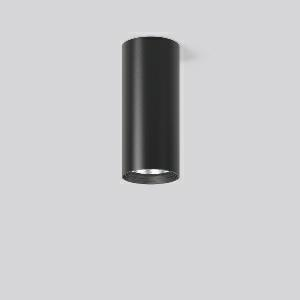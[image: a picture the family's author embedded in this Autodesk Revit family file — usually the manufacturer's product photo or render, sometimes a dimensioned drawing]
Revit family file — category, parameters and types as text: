
# Revit family: heledon_mini_a_931200_003_4768
name_source: partatom
category: Lighting Fixtures
units: mm (PartAtom-declared; Revit-internal decimal feet)

## family parameters
Cut with Voids When Loaded = No
Host = Face
Light Source = No
Part Type = Normal
Room Calculation Point = No
Round Connector Dimension = Use Diameter
Shared = No

## types (1)
- HELEDON mini A (1 x LED Modul 930, 2500 lm, 3000)
    Apparent Load = 20 VA
    Approval mark = CE
    CIE Flux Codes = 100 100 100 100 100
    Color Rendering = 90
    Color Temperature = 3000
    Default Elevation = 1800 mm
    Description = Series: HELEDON mini
Cylindrical surface-mounted downlight. Housing: die-cast aluminium, powder-coated. Internal ceiling frame polycarbonate with bayonet mounting. Black plastic ring and recessed LED to prevent glare from the side. Optical assembly with reflector made of MIRO-Silver with 98% total light reflection for outstanding efficiency - can be changed without tools. Best colour rendering index Ra>90. Suitable for Ceiling mounting. Easy installation with a separate ceiling frame with bayonet mounting and plug connection. Driver integrated. Connected via plug-in connector. High quality converter without flickering and stroboscopic effect. The following accessories can be mounted without use of tools: interchangeable lenses, decorative glasses, honeycomb louvre, clear and frosted diffusers, white interchangeable plastic ring. 
Colour: deep black, matt (RAL 9005)
Diameter: 87 mm
Height: 197 mm
Lamp: LED
Socket: without socket
Colour temperature: 3000K
Colour rendering index (CRI): 92
System power: 20 W
Rated luminous flux: 2500 lm
Luminous efficiency: 125 lm/W
Control gear: Regulated power supply
Protection class: I
Type of protection: IP 20
    Height = 197 mm
    Lamp = 1 x LED Modul 930
    Lamp Light Flux = 2500 lm
    Lamp count = 1
    Length = 87 mm
    Lifetime = 50000 h
    Luminous efficacy = 125 lm/W
    Manufacturer = RZB
    ModVariant = No
    Model = 931200.003
    Mounting Place = Ceiling
    Mounting Type = Surface mounted
    Number of Poles = 1
    OnlyDefault = Yes
    Power Factor = 1
    Product Name = HELEDON mini A
    Product group = Surface mounted downlights
    ProductGroupID = 302
    Protection Class = Protection class I
    Protection Degree = IP 20
    RLX_Detail_Level = 1
    RLX_Emergency_Light_Flux = 0 lm
    RLX_Emergency_Type = 0
    RLX_Emergency_Type_DB = No
    RlxData = <blob elided: 106245 chars, md5=6451e43d>
    Socket = socket
    Standby Power = 0 W
    System Light Flux = 2500 lm
    System Power = 20 W
    Type Comments = Product without accessories
    Type Image = 931188.003.jpg
    URL = http://relux.com
    VarID = ---
    Voltage = 230 V
    Voltage Range = 220-240 V
    Weight = 0.00 kg
    Width = 0 mm  [stored 0 ft]

note: [stored X ft] marks values corroborated as IEEE doubles in the binary element streams (Revit-internal decimal feet)

## geometry (parser evidence)
native form markers: Blend x4, Sweep x8
no freeform markers — native parametric forms only
